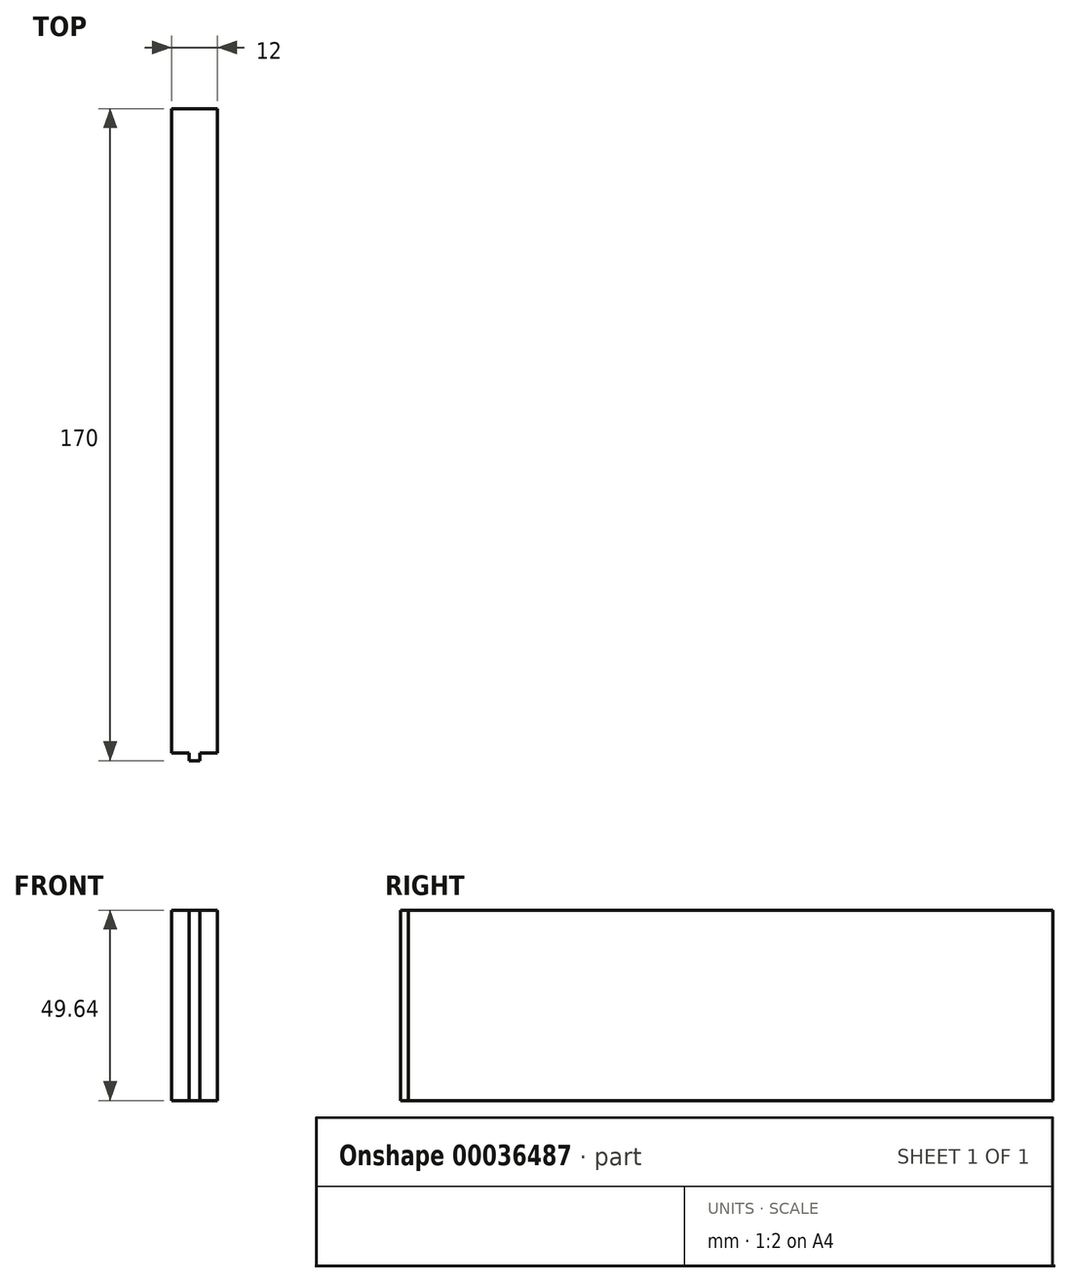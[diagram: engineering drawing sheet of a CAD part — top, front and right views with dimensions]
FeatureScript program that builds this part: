
annotation { "Feature Type Name" : "Feature", "Feature Type Description" : "" }
export const myFeature = defineFeature(function(context is Context, id is Id, definition is map)
    precondition{}
    {
        {
            var Q0;
            Q0=qCreatedBy(makeId("Right.planeOp"),FACE);
            var sketch = newSketch(context, id + "F0", { "sketchPlane" : qUnion([Q0])});
            skLineSegment(sketch, "E0.bottom", {"start": v(-84.88, 49.64) * mm, "end": v(83.12, 49.64) * mm});
            skLineSegment(sketch, "E0.top", {"start": v(-84.88, 0) * mm, "end": v(83.12, 0) * mm});
            skLineSegment(sketch, "E0.left", {"start": v(-84.88, 49.64) * mm, "end": v(-84.88, 0) * mm});
            skLineSegment(sketch, "E0.right", {"start": v(83.12, 49.64) * mm, "end": v(83.12, 0) * mm});
            skSolve(sketch);
        }
        {
            var Q0;
            Q0 = qSketchRegion(id + "F0", true);
            extrude(context, id + "F1", {"entities" : qUnion([Q0]), "depth" : 12 * mm});
        }
        {
            var Q0;
            Q0=makeQuery(id+"F1.opExtrude","SWEPT_FACE",FACE,{"disambiguationData":[OSD([sQuery(id+"F0.wireOp",EDGE,"E0.left")])]});
            var sketch = newSketch(context, id + "F2", { "sketchPlane" : qUnion([Q0])});
            skLineSegment(sketch, "E1.bottom", {"start": v(6, 49.64) * mm, "end": v(7.4, 49.64) * mm});
            skLineSegment(sketch, "E1.top", {"start": v(6, 0) * mm, "end": v(7.4, 0) * mm});
            skLineSegment(sketch, "E1.left", {"start": v(6, 49.64) * mm, "end": v(6, 0) * mm});
            skLineSegment(sketch, "E1.right", {"start": v(7.4, 49.64) * mm, "end": v(7.4, 0) * mm});
            skLineSegment(sketch, "E2.MirrorCS", {"start": v(4.6, 49.64) * mm, "end": v(4.6, 0) * mm});
            skSolve(sketch);
        }
        {
            var Q0;
            Q0=makeQuery(id+"F2.imprint","IMPRINT",FACE,{"disambiguationData":[TD([[makeQuery(id+"F2.imprint","IMPRINT",EDGE,{"derivedFrom":sQuery(id+"F2.wireOp",EDGE,"E1.bottom")}),1.0]])]});
            var Q1;
            {var subQ3=sQuery(id+"F2.wireOp",EDGE,"E1.left");Q1=makeQuery(id+"F2.imprint","IMPRINT",FACE,{"disambiguationData":[TD([[makeQuery(id+"F2.imprint","IMPRINT",EDGE,{"derivedFrom":subQ3}),-1.0]])]});}
            extrude(context, id + "F3", {"entities" : qUnion([Q0, Q1]), "operationType" : NewBodyOperationType.ADD, "depth" : 2 * mm});
        }
    });
